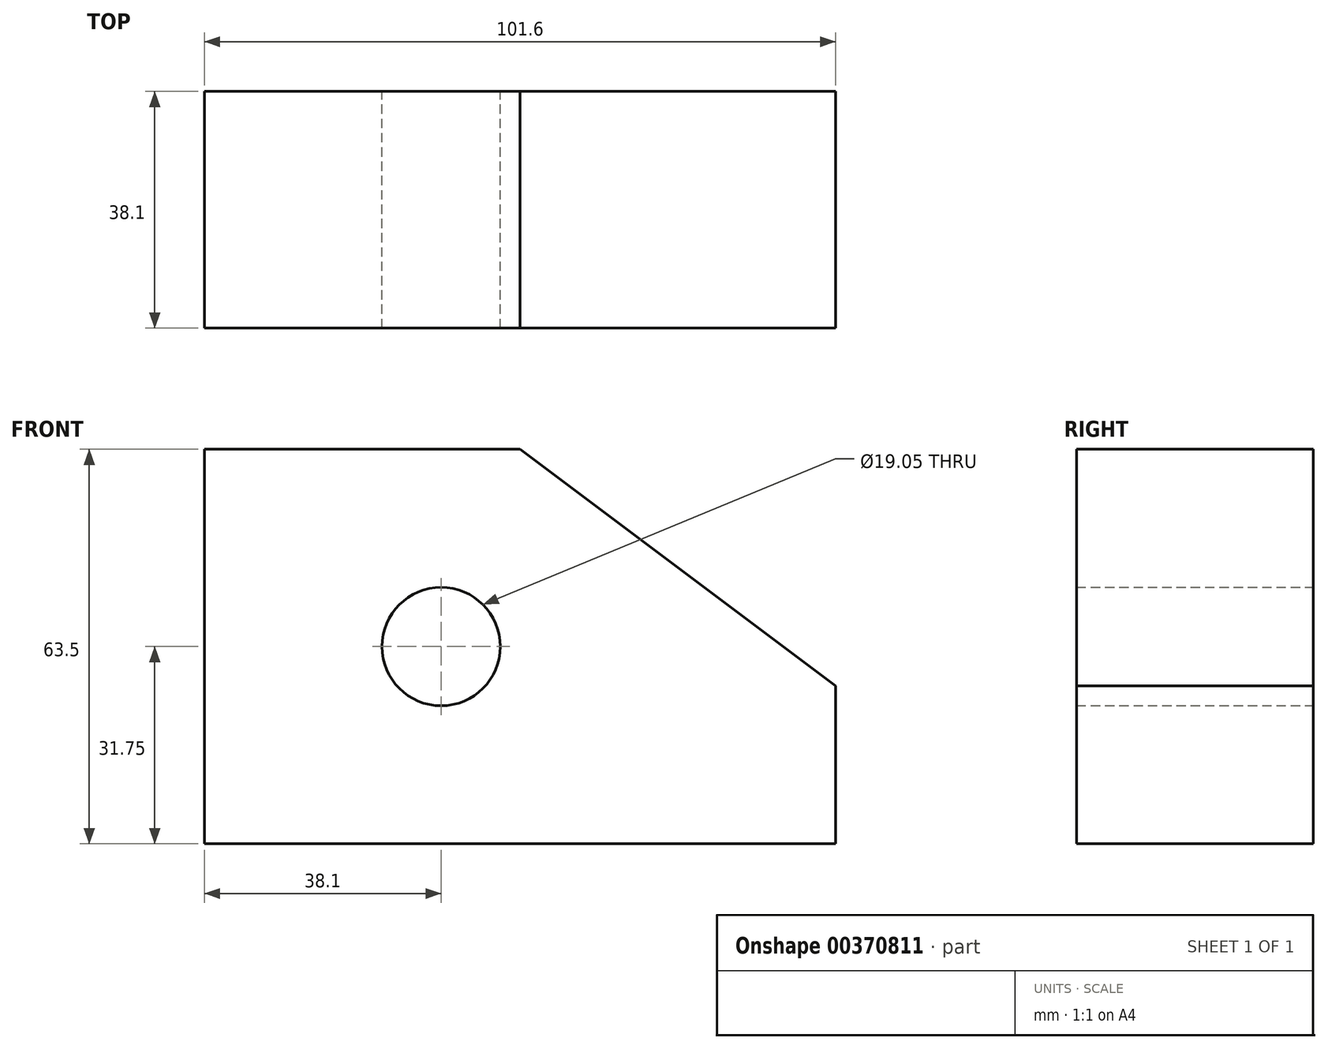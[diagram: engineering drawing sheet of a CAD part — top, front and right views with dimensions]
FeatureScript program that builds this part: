
annotation { "Feature Type Name" : "Feature", "Feature Type Description" : "" }
export const myFeature = defineFeature(function(context is Context, id is Id, definition is map)
    precondition{}
    {
        {
            var Q0;
            Q0=qCreatedBy(makeId("Front.planeOp"),FACE);
            var sketch = newSketch(context, id + "F0", { "sketchPlane" : qUnion([Q0])});
            skLineSegment(sketch, "E0", {"start": v(0, 0) * mm, "end": v(-50.8, 0) * mm});
            skLineSegment(sketch, "E1", {"start": v(-50.8, 0) * mm, "end": v(-50.8, -63.5) * mm});
            skLineSegment(sketch, "E2", {"start": v(-50.8, -63.5) * mm, "end": v(50.8, -63.5) * mm});
            skLineSegment(sketch, "E3", {"start": v(50.8, -63.5) * mm, "end": v(50.8, -38.1) * mm});
            skLineSegment(sketch, "E4", {"start": v(50.8, -38.1) * mm, "end": v(0, 0) * mm});
            skCircle(sketch, "E5", {"center": v(-12.7, -31.75) * mm, "radius": 9.53 * mm});
            skSolve(sketch);
        }
        {
            var Q0;
            Q0=makeQuery(id+"F0.imprint","IMPRINT",FACE,{"disambiguationData":[TD([[makeQuery(id+"F0.imprint","IMPRINT",EDGE,{"derivedFrom":sQuery(id+"F0.wireOp",EDGE,"E0")}),1.0]])]});
            extrude(context, id + "F1", {"entities" : qUnion([Q0]), "depth" : 38.1 * mm});
        }
    });
